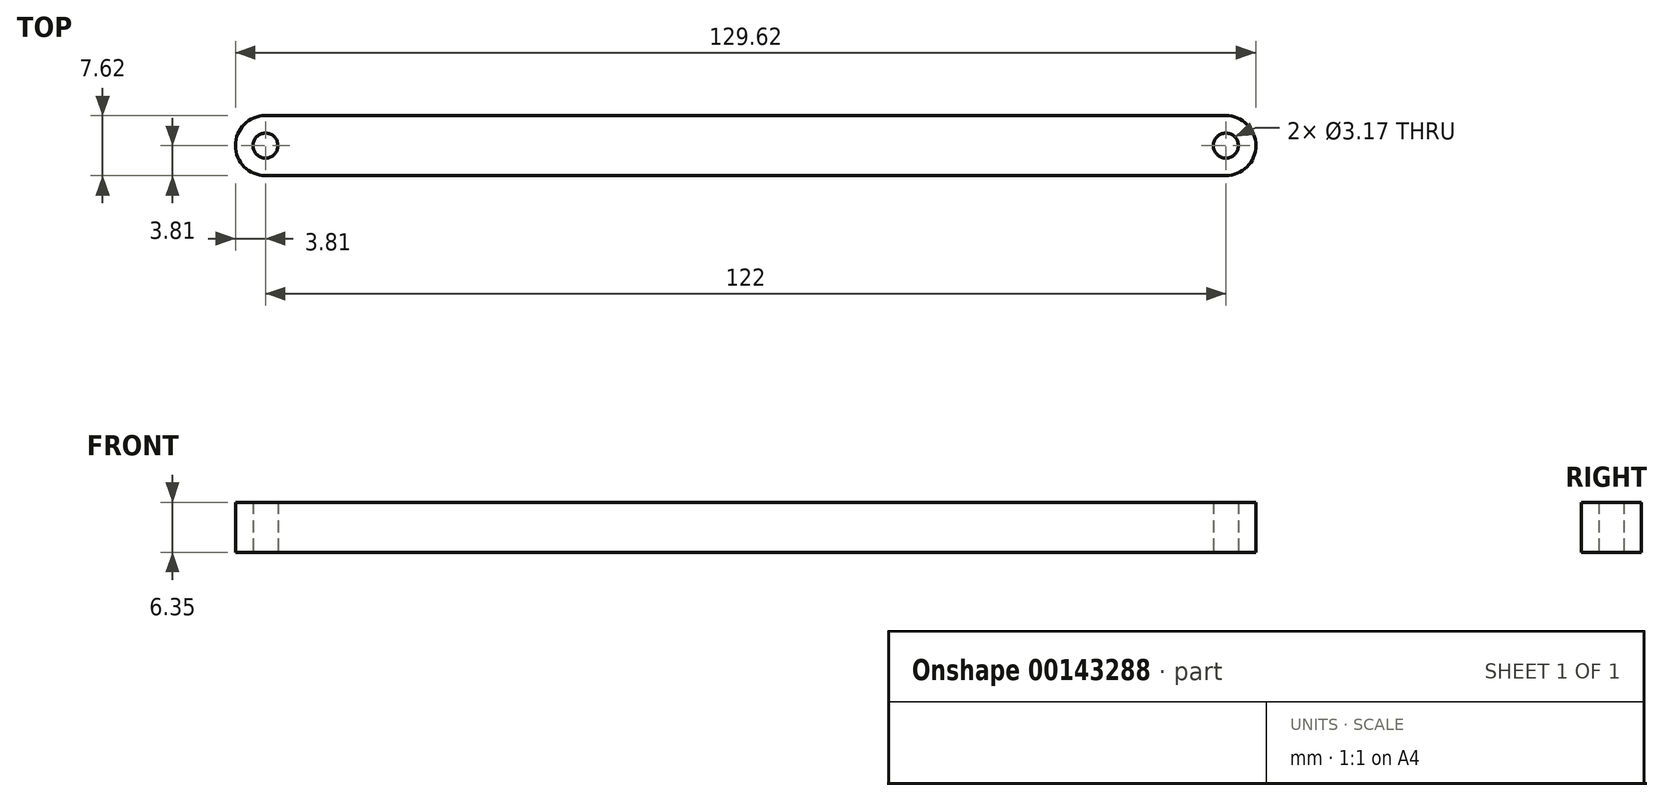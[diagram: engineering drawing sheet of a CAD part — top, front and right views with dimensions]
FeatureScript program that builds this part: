
annotation { "Feature Type Name" : "Feature", "Feature Type Description" : "" }
export const myFeature = defineFeature(function(context is Context, id is Id, definition is map)
    precondition{}
    {
        {
            var Q0;
            Q0=qCreatedBy(makeId("Top.planeOp"),FACE);
            var sketch = newSketch(context, id + "F0", { "sketchPlane" : qUnion([Q0])});
            skLineSegment(sketch, "E0", {"start": v(-61, 0) * mm, "end": v(61, 0) * mm});
            skLineSegment(sketch, "E1", {"start": v(61, 0) * mm, "end": v(-61, 0) * mm});
            skPoint(sketch, "E2", {"position": v(0, 0) * mm});
            skCircle(sketch, "E3", {"center": v(-61, 0) * mm, "radius": 1.59 * mm});
            skCircle(sketch, "E4", {"center": v(61, 0) * mm, "radius": 1.59 * mm});
            skLineSegment(sketch, "E5", {"start": v(-61, 3.81) * mm, "end": v(61, 3.81) * mm});
            skLineSegment(sketch, "E6", {"start": v(61, 3.8) * mm, "end": v(61, -3.8) * mm});
            skLineSegment(sketch, "E7", {"start": v(61, -3.8) * mm, "end": v(-61, -3.81) * mm});
            skLineSegment(sketch, "E8", {"start": v(-61, -3.81) * mm, "end": v(-61, 3.8) * mm});
            skArc(sketch, "E9", {"start": v(-61, 3.81) * mm, "mid": v(-64.81, 0) * mm, "end": v(-61, -3.81) * mm});
            skArc(sketch, "E10", {"start": v(61, -3.8) * mm, "mid": v(64.8, 0) * mm, "end": v(61, 3.81) * mm});
            skSolve(sketch);
        }
        {
            var Q0;
            Q0 = qSketchRegion(id + "F0", true);
            extrude(context, id + "F1", {"entities" : qUnion([Q0]), "depth" : 6.35 * mm, "offsetDistance" : 25.4 * mm});
        }
    });
